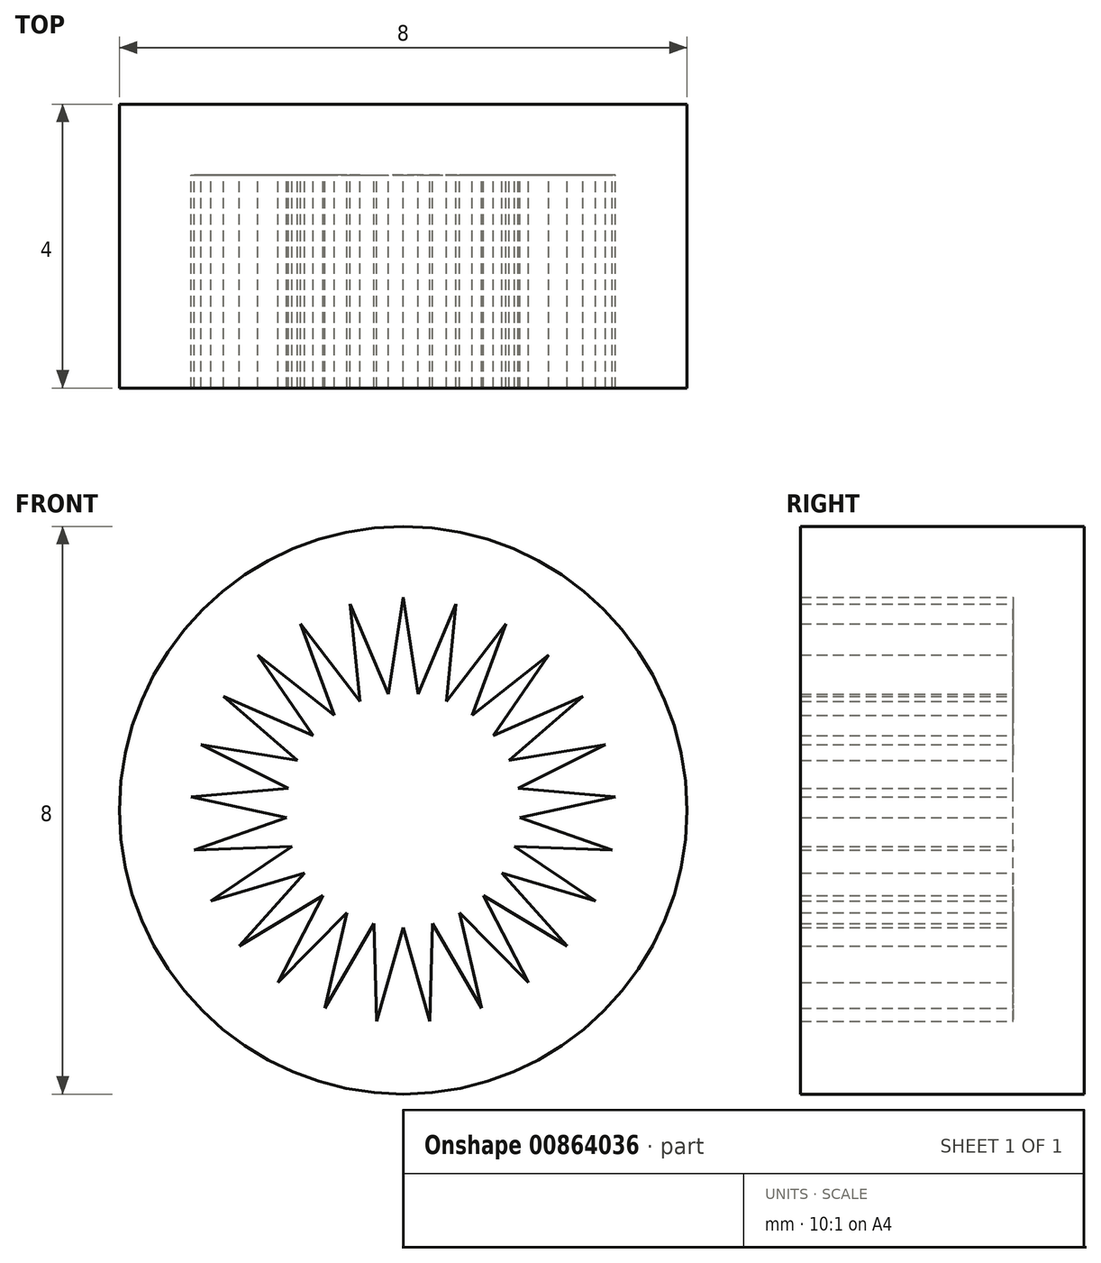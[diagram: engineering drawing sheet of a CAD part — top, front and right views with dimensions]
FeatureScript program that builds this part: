
annotation { "Feature Type Name" : "Feature", "Feature Type Description" : "" }
export const myFeature = defineFeature(function(context is Context, id is Id, definition is map)
    precondition{}
    {
        {
            var Q0;
            Q0=qCreatedBy(makeId("Front.planeOp"),FACE);
            var sketch = newSketch(context, id + "F0", { "sketchPlane" : qUnion([Q0])});
            skCircle(sketch, "E0", {"center": v(0, 0) * mm, "radius": 3 * mm});
            skCircle(sketch, "E1", {"center": v(0, 0) * mm, "radius": 4 * mm});
            skCircle(sketch, "E2", {"center": v(0, 0) * mm, "radius": 1.65 * mm});
            skCircle(sketch, "E3.cCircle", {"center": v(0, 0) * mm, "radius": 3 * mm, "construction": true});
            skCircle(sketch, "E4.cCircle", {"center": v(0, 0) * mm, "radius": 1.65 * mm, "construction": true});
            skLineSegment(sketch, "E4.0", {"start": v(0, -1.65) * mm, "end": v(-0.41, -1.6) * mm});
            skLineSegment(sketch, "E4.1", {"start": v(-0.41, -1.6) * mm, "end": v(-0.8, -1.45) * mm});
            skLineSegment(sketch, "E4.2", {"start": v(-0.8, -1.45) * mm, "end": v(-1.13, -1.2) * mm});
            skLineSegment(sketch, "E4.3", {"start": v(-1.13, -1.2) * mm, "end": v(-1.4, -0.88) * mm});
            skLineSegment(sketch, "E4.4", {"start": v(-1.4, -0.88) * mm, "end": v(-1.57, -0.5) * mm});
            skLineSegment(sketch, "E4.5", {"start": v(-1.57, -0.5) * mm, "end": v(-1.65, -0.1) * mm});
            skLineSegment(sketch, "E4.6", {"start": v(-1.65, -0.1) * mm, "end": v(-1.62, 0.3) * mm});
            skLineSegment(sketch, "E4.7", {"start": v(-1.62, 0.3) * mm, "end": v(-1.5, 0.7) * mm});
            skLineSegment(sketch, "E4.8", {"start": v(-1.5, 0.7) * mm, "end": v(-1.27, 1.05) * mm});
            skLineSegment(sketch, "E4.9", {"start": v(-1.27, 1.05) * mm, "end": v(-0.97, 1.33) * mm});
            skLineSegment(sketch, "E4.10", {"start": v(-0.97, 1.33) * mm, "end": v(-0.6, 1.53) * mm});
            skLineSegment(sketch, "E4.11", {"start": v(-0.6, 1.53) * mm, "end": v(-0.2, 1.64) * mm});
            skLineSegment(sketch, "E4.12", {"start": v(-0.2, 1.64) * mm, "end": v(0.2, 1.64) * mm});
            skLineSegment(sketch, "E4.13", {"start": v(0.2, 1.64) * mm, "end": v(0.6, 1.53) * mm});
            skLineSegment(sketch, "E4.14", {"start": v(0.6, 1.53) * mm, "end": v(0.97, 1.33) * mm});
            skLineSegment(sketch, "E4.15", {"start": v(0.97, 1.33) * mm, "end": v(1.27, 1.05) * mm});
            skLineSegment(sketch, "E4.16", {"start": v(1.27, 1.05) * mm, "end": v(1.5, 0.7) * mm});
            skLineSegment(sketch, "E4.17", {"start": v(1.5, 0.7) * mm, "end": v(1.62, 0.3) * mm});
            skLineSegment(sketch, "E4.18", {"start": v(1.62, 0.3) * mm, "end": v(1.65, -0.1) * mm});
            skLineSegment(sketch, "E4.19", {"start": v(1.65, -0.1) * mm, "end": v(1.57, -0.5) * mm});
            skLineSegment(sketch, "E4.20", {"start": v(1.57, -0.5) * mm, "end": v(1.4, -0.88) * mm});
            skLineSegment(sketch, "E4.21", {"start": v(1.4, -0.88) * mm, "end": v(1.13, -1.2) * mm});
            skLineSegment(sketch, "E4.22", {"start": v(1.13, -1.2) * mm, "end": v(0.8, -1.45) * mm});
            skLineSegment(sketch, "E4.23", {"start": v(0.8, -1.45) * mm, "end": v(0.41, -1.6) * mm});
            skLineSegment(sketch, "E4.24", {"start": v(0.41, -1.6) * mm, "end": v(0, -1.65) * mm});
            skLineSegment(sketch, "E5", {"start": v(0, 3) * mm, "end": v(-0.2, 1.64) * mm});
            skLineSegment(sketch, "E6", {"start": v(-0.75, 2.9) * mm, "end": v(-0.2, 1.64) * mm});
            skLineSegment(sketch, "E7", {"start": v(-0.75, 2.9) * mm, "end": v(-0.6, 1.53) * mm});
            skLineSegment(sketch, "E8", {"start": v(-0.6, 1.53) * mm, "end": v(-1.45, 2.63) * mm});
            skLineSegment(sketch, "E9", {"start": v(-1.45, 2.63) * mm, "end": v(-0.97, 1.33) * mm});
            skLineSegment(sketch, "E10", {"start": v(-0.97, 1.33) * mm, "end": v(-2.05, 2.19) * mm});
            skLineSegment(sketch, "E11", {"start": v(-2.05, 2.19) * mm, "end": v(-1.27, 1.05) * mm});
            skLineSegment(sketch, "E12", {"start": v(-1.27, 1.05) * mm, "end": v(-2.53, 1.6) * mm});
            skLineSegment(sketch, "E13", {"start": v(-2.53, 1.6) * mm, "end": v(-1.5, 0.7) * mm});
            skLineSegment(sketch, "E14", {"start": v(-1.5, 0.7) * mm, "end": v(-2.85, 0.93) * mm});
            skLineSegment(sketch, "E15", {"start": v(-2.85, 0.93) * mm, "end": v(-1.62, 0.3) * mm});
            skLineSegment(sketch, "E16", {"start": v(-1.62, 0.3) * mm, "end": v(-3, 0.19) * mm});
            skLineSegment(sketch, "E17", {"start": v(-3, 0.19) * mm, "end": v(-1.65, -0.1) * mm});
            skLineSegment(sketch, "E18", {"start": v(-1.65, -0.1) * mm, "end": v(-2.95, -0.56) * mm});
            skLineSegment(sketch, "E19", {"start": v(-2.95, -0.56) * mm, "end": v(-1.57, -0.5) * mm});
            skLineSegment(sketch, "E20", {"start": v(-1.57, -0.5) * mm, "end": v(-2.71, -1.28) * mm});
            skLineSegment(sketch, "E21", {"start": v(-2.71, -1.28) * mm, "end": v(-1.4, -0.88) * mm});
            skLineSegment(sketch, "E22", {"start": v(-1.4, -0.88) * mm, "end": v(-2.31, -1.91) * mm});
            skLineSegment(sketch, "E23", {"start": v(-2.31, -1.91) * mm, "end": v(-1.13, -1.2) * mm});
            skLineSegment(sketch, "E24", {"start": v(-1.13, -1.2) * mm, "end": v(-1.76, -2.43) * mm});
            skLineSegment(sketch, "E25", {"start": v(-1.76, -2.43) * mm, "end": v(-0.8, -1.45) * mm});
            skLineSegment(sketch, "E26", {"start": v(-0.8, -1.45) * mm, "end": v(-1.1, -2.79) * mm});
            skLineSegment(sketch, "E27", {"start": v(-1.1, -2.79) * mm, "end": v(-0.41, -1.6) * mm});
            skLineSegment(sketch, "E28", {"start": v(-0.41, -1.6) * mm, "end": v(-0.38, -2.98) * mm});
            skLineSegment(sketch, "E29", {"start": v(-0.38, -2.98) * mm, "end": v(0, -1.65) * mm});
            skLineSegment(sketch, "E30", {"start": v(0, -1.65) * mm, "end": v(0.38, -2.98) * mm});
            skLineSegment(sketch, "E31", {"start": v(0.38, -2.98) * mm, "end": v(0.41, -1.6) * mm});
            skLineSegment(sketch, "E32", {"start": v(0.41, -1.6) * mm, "end": v(1.1, -2.79) * mm});
            skLineSegment(sketch, "E33", {"start": v(1.1, -2.79) * mm, "end": v(0.8, -1.45) * mm});
            skLineSegment(sketch, "E34", {"start": v(0.8, -1.45) * mm, "end": v(1.76, -2.43) * mm});
            skLineSegment(sketch, "E35", {"start": v(1.76, -2.43) * mm, "end": v(1.13, -1.2) * mm});
            skLineSegment(sketch, "E36", {"start": v(1.13, -1.2) * mm, "end": v(2.31, -1.91) * mm});
            skLineSegment(sketch, "E37", {"start": v(2.31, -1.91) * mm, "end": v(1.4, -0.88) * mm});
            skLineSegment(sketch, "E38", {"start": v(1.4, -0.88) * mm, "end": v(2.71, -1.28) * mm});
            skLineSegment(sketch, "E39", {"start": v(2.71, -1.28) * mm, "end": v(1.57, -0.5) * mm});
            skLineSegment(sketch, "E40", {"start": v(1.57, -0.5) * mm, "end": v(2.95, -0.56) * mm});
            skLineSegment(sketch, "E41", {"start": v(2.95, -0.56) * mm, "end": v(1.65, -0.1) * mm});
            skLineSegment(sketch, "E42", {"start": v(1.65, -0.1) * mm, "end": v(3, 0.19) * mm});
            skLineSegment(sketch, "E43", {"start": v(3, 0.19) * mm, "end": v(1.62, 0.3) * mm});
            skLineSegment(sketch, "E44", {"start": v(1.62, 0.3) * mm, "end": v(2.85, 0.93) * mm});
            skLineSegment(sketch, "E45", {"start": v(2.85, 0.93) * mm, "end": v(1.5, 0.7) * mm});
            skLineSegment(sketch, "E46", {"start": v(1.5, 0.7) * mm, "end": v(2.53, 1.6) * mm});
            skLineSegment(sketch, "E47", {"start": v(2.53, 1.6) * mm, "end": v(1.27, 1.05) * mm});
            skLineSegment(sketch, "E48", {"start": v(1.27, 1.05) * mm, "end": v(2.05, 2.19) * mm});
            skLineSegment(sketch, "E49", {"start": v(2.05, 2.19) * mm, "end": v(0.97, 1.33) * mm});
            skLineSegment(sketch, "E50", {"start": v(0.97, 1.33) * mm, "end": v(1.45, 2.63) * mm});
            skLineSegment(sketch, "E51", {"start": v(1.45, 2.63) * mm, "end": v(0.6, 1.53) * mm});
            skLineSegment(sketch, "E52", {"start": v(0.6, 1.53) * mm, "end": v(0.75, 2.9) * mm});
            skLineSegment(sketch, "E53", {"start": v(0.75, 2.9) * mm, "end": v(0.2, 1.64) * mm});
            skLineSegment(sketch, "E54", {"start": v(0.2, 1.64) * mm, "end": v(0, 3) * mm});
            skSolve(sketch);
        }
        {
            var Q0;
            Q0=makeQuery(id+"F0.imprint","IMPRINT",FACE,{"disambiguationData":[TD([[makeQuery(id+"F0.imprint","IMPRINT",EDGE,{"derivedFrom":sQuery(id+"F0.wireOp",EDGE,"E1")}),1.0]])]});
            var Q1;
            {var subQ0=sQuery(id+"F0.wireOp",EDGE,"191f228b-e5a5-47d5-a300-bf6d3b310172");Q1=makeQuery(id+"F0.imprint","IMPRINT",FACE,{"disambiguationData":[TD([[makeQuery(id+"F0.imprint","IMPRINT",EDGE,{"derivedFrom":subQ0}),-1.0]])]});}
            var Q2;
            {var subQ0=sQuery(id+"F0.wireOp",EDGE,"1723c25a-e232-420a-af23-11f6e1e45479");Q2=makeQuery(id+"F0.imprint","IMPRINT",FACE,{"disambiguationData":[TD([[makeQuery(id+"F0.imprint","IMPRINT",EDGE,{"derivedFrom":subQ0}),-1.0]])]});}
            var Q3;
            {var subQ0=sQuery(id+"F0.wireOp",EDGE,"362b071b-b4e2-4c32-97d3-f70041ff60b6");Q3=makeQuery(id+"F0.imprint","IMPRINT",FACE,{"disambiguationData":[TD([[makeQuery(id+"F0.imprint","IMPRINT",EDGE,{"derivedFrom":subQ0}),1.0]])]});}
            var Q4;
            {var subQ0=sQuery(id+"F0.wireOp",EDGE,"7a3e42e3-73c9-4e71-a878-db48f86a027f");Q4=makeQuery(id+"F0.imprint","IMPRINT",FACE,{"disambiguationData":[TD([[makeQuery(id+"F0.imprint","IMPRINT",EDGE,{"derivedFrom":subQ0}),1.0]])]});}
            var Q5;
            {var subQ0=sQuery(id+"F0.wireOp",EDGE,"a710b964-fec3-4947-b213-2410728157db");Q5=makeQuery(id+"F0.imprint","IMPRINT",FACE,{"disambiguationData":[TD([[makeQuery(id+"F0.imprint","IMPRINT",EDGE,{"derivedFrom":subQ0}),1.0]])]});}
            var Q6;
            {var subQ0=sQuery(id+"F0.wireOp",EDGE,"60680273-4920-44da-8bc3-3f6f87752808");Q6=makeQuery(id+"F0.imprint","IMPRINT",FACE,{"disambiguationData":[TD([[makeQuery(id+"F0.imprint","IMPRINT",EDGE,{"derivedFrom":subQ0}),1.0]])]});}
            var Q7;
            {var subQ0=sQuery(id+"F0.wireOp",EDGE,"2f8d73f0-317a-4c88-aaee-1b2851b7c96e");Q7=makeQuery(id+"F0.imprint","IMPRINT",FACE,{"disambiguationData":[TD([[makeQuery(id+"F0.imprint","IMPRINT",EDGE,{"derivedFrom":subQ0}),1.0]])]});}
            var Q8;
            {var subQ0=sQuery(id+"F0.wireOp",EDGE,"349960dc-c3b8-4aa2-95a6-2044da98fb72");Q8=makeQuery(id+"F0.imprint","IMPRINT",FACE,{"disambiguationData":[TD([[makeQuery(id+"F0.imprint","IMPRINT",EDGE,{"derivedFrom":subQ0}),1.0]])]});}
            var Q9;
            {var subQ0=sQuery(id+"F0.wireOp",EDGE,"c7be37dc-6ee6-451d-a77f-0cf4add8b74c");Q9=makeQuery(id+"F0.imprint","IMPRINT",FACE,{"disambiguationData":[TD([[makeQuery(id+"F0.imprint","IMPRINT",EDGE,{"derivedFrom":subQ0}),1.0]])]});}
            var Q10;
            {var subQ0=sQuery(id+"F0.wireOp",EDGE,"4aff2ad2-ea2a-4098-8c14-60c1d9ab17a0");Q10=makeQuery(id+"F0.imprint","IMPRINT",FACE,{"disambiguationData":[TD([[makeQuery(id+"F0.imprint","IMPRINT",EDGE,{"derivedFrom":subQ0}),-1.0]])]});}
            var Q11;
            {var subQ0=sQuery(id+"F0.wireOp",EDGE,"2e92db5d-52d9-4a2f-acd0-dec73ec550c8");Q11=makeQuery(id+"F0.imprint","IMPRINT",FACE,{"disambiguationData":[TD([[makeQuery(id+"F0.imprint","IMPRINT",EDGE,{"derivedFrom":subQ0}),-1.0]])]});}
            var Q12;
            {var subQ0=sQuery(id+"F0.wireOp",EDGE,"9941dce6-5cf8-40e4-90cd-53aa257fbfa3");Q12=makeQuery(id+"F0.imprint","IMPRINT",FACE,{"disambiguationData":[TD([[makeQuery(id+"F0.imprint","IMPRINT",EDGE,{"derivedFrom":subQ0}),-1.0]])]});}
            var Q13;
            {var subQ2=sQuery(id+"F0.wireOp",EDGE,"aa89b7cd-d551-4e84-b0b1-1e06fde4f388");Q13=makeQuery(id+"F0.imprint","IMPRINT",FACE,{"disambiguationData":[TD([[makeQuery(id+"F0.imprint","IMPRINT",EDGE,{"derivedFrom":subQ2}),1.0]])]});}
            var Q14;
            {var subQ0=sQuery(id+"F0.wireOp",EDGE,"cc53d425-3ef8-4edf-87f2-34f36bc6dec7");Q14=makeQuery(id+"F0.imprint","IMPRINT",FACE,{"disambiguationData":[TD([[makeQuery(id+"F0.imprint","IMPRINT",EDGE,{"derivedFrom":subQ0}),1.0]])]});}
            var Q15;
            {var subQ0=sQuery(id+"F0.wireOp",EDGE,"99681175-5654-4388-8651-d3d52a13e443");Q15=makeQuery(id+"F0.imprint","IMPRINT",FACE,{"disambiguationData":[TD([[makeQuery(id+"F0.imprint","IMPRINT",EDGE,{"derivedFrom":subQ0}),1.0]])]});}
            var Q16;
            {var subQ0=sQuery(id+"F0.wireOp",EDGE,"2ca4b1c5-08c9-43bc-8a30-41003a56ef57");Q16=makeQuery(id+"F0.imprint","IMPRINT",FACE,{"disambiguationData":[TD([[makeQuery(id+"F0.imprint","IMPRINT",EDGE,{"derivedFrom":subQ0}),1.0]])]});}
            var Q17;
            {var subQ0=sQuery(id+"F0.wireOp",EDGE,"d3c2645e-955d-4a5b-9ae6-9eed4a245719");Q17=makeQuery(id+"F0.imprint","IMPRINT",FACE,{"disambiguationData":[TD([[makeQuery(id+"F0.imprint","IMPRINT",EDGE,{"derivedFrom":subQ0}),1.0]])]});}
            var Q18;
            {var subQ0=sQuery(id+"F0.wireOp",EDGE,"d3f6a87d-8e7b-4a19-8049-f323434571ec");Q18=makeQuery(id+"F0.imprint","IMPRINT",FACE,{"disambiguationData":[TD([[makeQuery(id+"F0.imprint","IMPRINT",EDGE,{"derivedFrom":subQ0}),1.0]])]});}
            var Q19;
            {var subQ0=sQuery(id+"F0.wireOp",EDGE,"589032c6-bdc8-48a5-8756-f54bf3a24945");Q19=makeQuery(id+"F0.imprint","IMPRINT",FACE,{"disambiguationData":[TD([[makeQuery(id+"F0.imprint","IMPRINT",EDGE,{"derivedFrom":subQ0}),1.0]])]});}
            var Q20;
            {var subQ0=sQuery(id+"F0.wireOp",EDGE,"12f93d1c-aee5-4c1c-92fe-329b828fc1ab");Q20=makeQuery(id+"F0.imprint","IMPRINT",FACE,{"disambiguationData":[TD([[makeQuery(id+"F0.imprint","IMPRINT",EDGE,{"derivedFrom":subQ0}),1.0]])]});}
            var Q21;
            {var subQ0=sQuery(id+"F0.wireOp",EDGE,"b9c6a9d8-4597-4bf0-9964-2ef2b3ef8dc4");Q21=makeQuery(id+"F0.imprint","IMPRINT",FACE,{"disambiguationData":[TD([[makeQuery(id+"F0.imprint","IMPRINT",EDGE,{"derivedFrom":subQ0}),1.0]])]});}
            var Q22;
            {var subQ0=sQuery(id+"F0.wireOp",EDGE,"6288aacb-8e0d-4685-9329-790f9a596c2f");Q22=makeQuery(id+"F0.imprint","IMPRINT",FACE,{"disambiguationData":[TD([[makeQuery(id+"F0.imprint","IMPRINT",EDGE,{"derivedFrom":subQ0}),1.0]])]});}
            var Q23;
            {var subQ0=sQuery(id+"F0.wireOp",EDGE,"50311a24-d9df-4292-b5ea-d22f6d0c8ad2");Q23=makeQuery(id+"F0.imprint","IMPRINT",FACE,{"disambiguationData":[TD([[makeQuery(id+"F0.imprint","IMPRINT",EDGE,{"derivedFrom":subQ0}),1.0]])]});}
            var Q24;
            {var subQ0=sQuery(id+"F0.wireOp",EDGE,"c8f29483-0d33-4b23-b36e-bf183a1a309b");Q24=makeQuery(id+"F0.imprint","IMPRINT",FACE,{"disambiguationData":[TD([[makeQuery(id+"F0.imprint","IMPRINT",EDGE,{"derivedFrom":subQ0}),1.0]])]});}
            var Q25;
            {var subQ0=sQuery(id+"F0.wireOp",EDGE,"e2a48b54-4f9e-43bf-ae69-ea60452bf6d6");Q25=makeQuery(id+"F0.imprint","IMPRINT",FACE,{"disambiguationData":[TD([[makeQuery(id+"F0.imprint","IMPRINT",EDGE,{"derivedFrom":subQ0}),1.0]])]});}
            var Q26;
            Q26=makeQuery(id+"F0.imprint","IMPRINT",FACE,{"disambiguationData":[TD([[makeQuery(id+"F0.imprint","IMPRINT",EDGE,{"derivedFrom":sQuery(id+"F0.wireOp",EDGE,"E3.19")}),-1.0]])]});
            var Q27;
            Q27=makeQuery(id+"F0.imprint","IMPRINT",FACE,{"disambiguationData":[TD([[makeQuery(id+"F0.imprint","IMPRINT",EDGE,{"derivedFrom":sQuery(id+"F0.wireOp",EDGE,"E3.18")}),-1.0]])]});
            var Q28;
            Q28=makeQuery(id+"F0.imprint","IMPRINT",FACE,{"disambiguationData":[TD([[makeQuery(id+"F0.imprint","IMPRINT",EDGE,{"derivedFrom":sQuery(id+"F0.wireOp",EDGE,"E3.21")}),-1.0]])]});
            var Q29;
            Q29=makeQuery(id+"F0.imprint","IMPRINT",FACE,{"disambiguationData":[TD([[makeQuery(id+"F0.imprint","IMPRINT",EDGE,{"derivedFrom":sQuery(id+"F0.wireOp",EDGE,"E3.22")}),-1.0]])]});
            var Q30;
            Q30=makeQuery(id+"F0.imprint","IMPRINT",FACE,{"disambiguationData":[TD([[makeQuery(id+"F0.imprint","IMPRINT",EDGE,{"derivedFrom":sQuery(id+"F0.wireOp",EDGE,"E3.23")}),-1.0]])]});
            var Q31;
            Q31=makeQuery(id+"F0.imprint","IMPRINT",FACE,{"disambiguationData":[TD([[makeQuery(id+"F0.imprint","IMPRINT",EDGE,{"derivedFrom":sQuery(id+"F0.wireOp",EDGE,"E3.20")}),-1.0]])]});
            var Q32;
            Q32=makeQuery(id+"F0.imprint","IMPRINT",FACE,{"disambiguationData":[TD([[makeQuery(id+"F0.imprint","IMPRINT",EDGE,{"derivedFrom":sQuery(id+"F0.wireOp",EDGE,"E3.17")}),-1.0]])]});
            var Q33;
            Q33=makeQuery(id+"F0.imprint","IMPRINT",FACE,{"disambiguationData":[TD([[makeQuery(id+"F0.imprint","IMPRINT",EDGE,{"derivedFrom":sQuery(id+"F0.wireOp",EDGE,"E3.15")}),-1.0]])]});
            var Q34;
            Q34=makeQuery(id+"F0.imprint","IMPRINT",FACE,{"disambiguationData":[TD([[makeQuery(id+"F0.imprint","IMPRINT",EDGE,{"derivedFrom":sQuery(id+"F0.wireOp",EDGE,"E3.16")}),-1.0]])]});
            var Q35;
            Q35=makeQuery(id+"F0.imprint","IMPRINT",FACE,{"disambiguationData":[TD([[makeQuery(id+"F0.imprint","IMPRINT",EDGE,{"derivedFrom":sQuery(id+"F0.wireOp",EDGE,"E3.14")}),-1.0]])]});
            var Q36;
            Q36=makeQuery(id+"F0.imprint","IMPRINT",FACE,{"disambiguationData":[TD([[makeQuery(id+"F0.imprint","IMPRINT",EDGE,{"derivedFrom":sQuery(id+"F0.wireOp",EDGE,"E3.13")}),-1.0]])]});
            var Q37;
            Q37=makeQuery(id+"F0.imprint","IMPRINT",FACE,{"disambiguationData":[TD([[makeQuery(id+"F0.imprint","IMPRINT",EDGE,{"derivedFrom":sQuery(id+"F0.wireOp",EDGE,"E3.12")}),-1.0]])]});
            var Q38;
            Q38=makeQuery(id+"F0.imprint","IMPRINT",FACE,{"disambiguationData":[TD([[makeQuery(id+"F0.imprint","IMPRINT",EDGE,{"derivedFrom":sQuery(id+"F0.wireOp",EDGE,"E3.11")}),-1.0]])]});
            var Q39;
            Q39=makeQuery(id+"F0.imprint","IMPRINT",FACE,{"disambiguationData":[TD([[makeQuery(id+"F0.imprint","IMPRINT",EDGE,{"derivedFrom":sQuery(id+"F0.wireOp",EDGE,"E3.10")}),-1.0]])]});
            var Q40;
            Q40=makeQuery(id+"F0.imprint","IMPRINT",FACE,{"disambiguationData":[TD([[makeQuery(id+"F0.imprint","IMPRINT",EDGE,{"derivedFrom":sQuery(id+"F0.wireOp",EDGE,"E3.9")}),-1.0]])]});
            var Q41;
            Q41=makeQuery(id+"F0.imprint","IMPRINT",FACE,{"disambiguationData":[TD([[makeQuery(id+"F0.imprint","IMPRINT",EDGE,{"derivedFrom":sQuery(id+"F0.wireOp",EDGE,"E3.8")}),-1.0]])]});
            var Q42;
            Q42=makeQuery(id+"F0.imprint","IMPRINT",FACE,{"disambiguationData":[TD([[makeQuery(id+"F0.imprint","IMPRINT",EDGE,{"derivedFrom":sQuery(id+"F0.wireOp",EDGE,"E3.7")}),-1.0]])]});
            var Q43;
            Q43=makeQuery(id+"F0.imprint","IMPRINT",FACE,{"disambiguationData":[TD([[makeQuery(id+"F0.imprint","IMPRINT",EDGE,{"derivedFrom":sQuery(id+"F0.wireOp",EDGE,"E3.6")}),-1.0]])]});
            var Q44;
            Q44=makeQuery(id+"F0.imprint","IMPRINT",FACE,{"disambiguationData":[TD([[makeQuery(id+"F0.imprint","IMPRINT",EDGE,{"derivedFrom":sQuery(id+"F0.wireOp",EDGE,"E3.5")}),-1.0]])]});
            var Q45;
            Q45=makeQuery(id+"F0.imprint","IMPRINT",FACE,{"disambiguationData":[TD([[makeQuery(id+"F0.imprint","IMPRINT",EDGE,{"derivedFrom":sQuery(id+"F0.wireOp",EDGE,"E3.4")}),-1.0]])]});
            var Q46;
            Q46=makeQuery(id+"F0.imprint","IMPRINT",FACE,{"disambiguationData":[TD([[makeQuery(id+"F0.imprint","IMPRINT",EDGE,{"derivedFrom":sQuery(id+"F0.wireOp",EDGE,"E3.3")}),-1.0]])]});
            var Q47;
            Q47=makeQuery(id+"F0.imprint","IMPRINT",FACE,{"disambiguationData":[TD([[makeQuery(id+"F0.imprint","IMPRINT",EDGE,{"derivedFrom":sQuery(id+"F0.wireOp",EDGE,"E3.2")}),-1.0]])]});
            var Q48;
            Q48=makeQuery(id+"F0.imprint","IMPRINT",FACE,{"disambiguationData":[TD([[makeQuery(id+"F0.imprint","IMPRINT",EDGE,{"derivedFrom":sQuery(id+"F0.wireOp",EDGE,"E3.0")}),-1.0]])]});
            var Q49;
            Q49=makeQuery(id+"F0.imprint","IMPRINT",FACE,{"disambiguationData":[TD([[makeQuery(id+"F0.imprint","IMPRINT",EDGE,{"derivedFrom":sQuery(id+"F0.wireOp",EDGE,"E3.24")}),-1.0]])]});
            var Q50;
            Q50=makeQuery(id+"F0.imprint","IMPRINT",FACE,{"disambiguationData":[TD([[makeQuery(id+"F0.imprint","IMPRINT",EDGE,{"derivedFrom":sQuery(id+"F0.wireOp",EDGE,"E3.1")}),-1.0]])]});
            var Q51;
            {var subQ0=sQuery(id+"F0.wireOp",EDGE,"E7");Q51=makeQuery(id+"F0.imprint","IMPRINT",FACE,{"disambiguationData":[TD([[makeQuery(id+"F0.imprint","IMPRINT",EDGE,{"derivedFrom":subQ0}),-1.0]])]});}
            var Q52;
            {var subQ0=sQuery(id+"F0.wireOp",EDGE,"E9");Q52=makeQuery(id+"F0.imprint","IMPRINT",FACE,{"disambiguationData":[TD([[makeQuery(id+"F0.imprint","IMPRINT",EDGE,{"derivedFrom":subQ0}),-1.0]])]});}
            var Q53;
            {var subQ0=sQuery(id+"F0.wireOp",EDGE,"E11");Q53=makeQuery(id+"F0.imprint","IMPRINT",FACE,{"disambiguationData":[TD([[makeQuery(id+"F0.imprint","IMPRINT",EDGE,{"derivedFrom":subQ0}),-1.0]])]});}
            var Q54;
            {var subQ0=sQuery(id+"F0.wireOp",EDGE,"E5");Q54=makeQuery(id+"F0.imprint","IMPRINT",FACE,{"disambiguationData":[TD([[makeQuery(id+"F0.imprint","IMPRINT",EDGE,{"derivedFrom":subQ0}),-1.0]])]});}
            var Q55;
            {var subQ2=sQuery(id+"F0.wireOp",EDGE,"E53");Q55=makeQuery(id+"F0.imprint","IMPRINT",FACE,{"disambiguationData":[TD([[makeQuery(id+"F0.imprint","IMPRINT",EDGE,{"derivedFrom":subQ2}),-1.0]])]});}
            var Q56;
            {var subQ0=sQuery(id+"F0.wireOp",EDGE,"E51");Q56=makeQuery(id+"F0.imprint","IMPRINT",FACE,{"disambiguationData":[TD([[makeQuery(id+"F0.imprint","IMPRINT",EDGE,{"derivedFrom":subQ0}),-1.0]])]});}
            var Q57;
            {var subQ0=sQuery(id+"F0.wireOp",EDGE,"E49");Q57=makeQuery(id+"F0.imprint","IMPRINT",FACE,{"disambiguationData":[TD([[makeQuery(id+"F0.imprint","IMPRINT",EDGE,{"derivedFrom":subQ0}),-1.0]])]});}
            extrude(context, id + "F1", {"entities" : qUnion([Q0, Q1, Q2, Q3, Q4, Q5, Q6, Q7, Q8, Q9, Q10, Q11, Q12, Q13, Q14, Q15, Q16, Q17, Q18, Q19, Q20, Q21, Q22, Q23, Q24, Q25, Q26, Q27, Q28, Q29, Q30, Q31, Q32, Q33, Q34, Q35, Q36, Q37, Q38, Q39, Q40, Q41, Q42, Q43, Q44, Q45, Q46, Q47, Q48, Q49, Q50, Q51, Q52, Q53, Q54, Q55, Q56, Q57]), "depth" : 3 * mm, "offsetDistance" : 25 * mm});
        }
        {
            var Q0;
            Q0=makeQuery(id+"F1.opExtrude","SWEPT_BODY",BODY,{"disambiguationData":[OSD([sQuery(id+"F0.wireOp",EDGE,"1723c25a-e232-420a-af23-11f6e1e45479"),sQuery(id+"F0.wireOp",EDGE,"5295c6c6-52b0-4e9a-9c64-aa566c587db1"),sQuery(id+"F0.wireOp",EDGE,"191f228b-e5a5-47d5-a300-bf6d3b310172"),sQuery(id+"F0.wireOp",EDGE,"cf70ef10-be83-42a8-b998-76c03f429467"),sQuery(id+"F0.wireOp",EDGE,"2e92db5d-52d9-4a2f-acd0-dec73ec550c8"),sQuery(id+"F0.wireOp",EDGE,"8a1419a8-a6e0-4fe3-8ad0-2659a204953f"),sQuery(id+"F0.wireOp",EDGE,"9941dce6-5cf8-40e4-90cd-53aa257fbfa3"),sQuery(id+"F0.wireOp",EDGE,"38f36d66-5889-4d61-b17e-66de369334f1"),sQuery(id+"F0.wireOp",EDGE,"362b071b-b4e2-4c32-97d3-f70041ff60b6"),sQuery(id+"F0.wireOp",EDGE,"a209e0ad-c9d0-4362-9147-c419651424fc"),sQuery(id+"F0.wireOp",EDGE,"7a3e42e3-73c9-4e71-a878-db48f86a027f"),sQuery(id+"F0.wireOp",EDGE,"a177d376-87b9-463b-93ab-41dd6348bae0"),sQuery(id+"F0.wireOp",EDGE,"a710b964-fec3-4947-b213-2410728157db"),sQuery(id+"F0.wireOp",EDGE,"1ebe16a6-329b-423c-8d02-a690ea02e21a"),sQuery(id+"F0.wireOp",EDGE,"60680273-4920-44da-8bc3-3f6f87752808"),sQuery(id+"F0.wireOp",EDGE,"07a1d955-efb7-4b04-82f9-21b5b055ff9c"),sQuery(id+"F0.wireOp",EDGE,"2f8d73f0-317a-4c88-aaee-1b2851b7c96e"),sQuery(id+"F0.wireOp",EDGE,"177c940f-3e80-47e4-9597-e37eb8e28c60"),sQuery(id+"F0.wireOp",EDGE,"349960dc-c3b8-4aa2-95a6-2044da98fb72"),sQuery(id+"F0.wireOp",EDGE,"f5aa7e73-0121-4040-9320-5db813b2d3bf"),sQuery(id+"F0.wireOp",EDGE,"c7be37dc-6ee6-451d-a77f-0cf4add8b74c"),sQuery(id+"F0.wireOp",EDGE,"97bad7f0-ba5f-4ffa-8f54-a637fe049995"),sQuery(id+"F0.wireOp",EDGE,"4aff2ad2-ea2a-4098-8c14-60c1d9ab17a0"),sQuery(id+"F0.wireOp",EDGE,"d753e143-b6aa-4dee-8de6-cae75ad036f2"),sQuery(id+"F0.wireOp",EDGE,"c8f29483-0d33-4b23-b36e-bf183a1a309b"),sQuery(id+"F0.wireOp",EDGE,"5b43d50d-1a8e-48e3-af0a-1195e99f841e"),sQuery(id+"F0.wireOp",EDGE,"e2a48b54-4f9e-43bf-ae69-ea60452bf6d6"),sQuery(id+"F0.wireOp",EDGE,"42233fef-6dd1-45c1-8fd8-0da537e6c1f3"),sQuery(id+"F0.wireOp",EDGE,"50311a24-d9df-4292-b5ea-d22f6d0c8ad2"),sQuery(id+"F0.wireOp",EDGE,"ddcee8d9-d30e-4910-9338-453dcf5c318e"),sQuery(id+"F0.wireOp",EDGE,"6288aacb-8e0d-4685-9329-790f9a596c2f"),sQuery(id+"F0.wireOp",EDGE,"b9c6a9d8-4597-4bf0-9964-2ef2b3ef8dc4"),sQuery(id+"F0.wireOp",EDGE,"9c044d92-1709-44a8-9e80-cc68e6d8e250"),sQuery(id+"F0.wireOp",EDGE,"7d94632d-f1b4-4678-813c-0d22cf0914ea"),sQuery(id+"F0.wireOp",EDGE,"12f93d1c-aee5-4c1c-92fe-329b828fc1ab"),sQuery(id+"F0.wireOp",EDGE,"b0bde724-e130-4cb4-bfe0-c640ccf8bd66"),sQuery(id+"F0.wireOp",EDGE,"589032c6-bdc8-48a5-8756-f54bf3a24945"),sQuery(id+"F0.wireOp",EDGE,"6b624495-a022-44ef-bb31-4b2f9aca960f"),sQuery(id+"F0.wireOp",EDGE,"d3f6a87d-8e7b-4a19-8049-f323434571ec"),sQuery(id+"F0.wireOp",EDGE,"bc16c7f2-d393-49ba-aa83-d674c351c39c"),sQuery(id+"F0.wireOp",EDGE,"d3c2645e-955d-4a5b-9ae6-9eed4a245719"),sQuery(id+"F0.wireOp",EDGE,"6b5cc574-cdc1-46be-bbed-f7c8129c668f"),sQuery(id+"F0.wireOp",EDGE,"2ca4b1c5-08c9-43bc-8a30-41003a56ef57"),sQuery(id+"F0.wireOp",EDGE,"21c57bb4-7a4b-46c3-846a-edf095b63d1c"),sQuery(id+"F0.wireOp",EDGE,"99681175-5654-4388-8651-d3d52a13e443"),sQuery(id+"F0.wireOp",EDGE,"40837eb8-84b9-4c3f-ab84-b3bfe63bb642"),sQuery(id+"F0.wireOp",EDGE,"cc53d425-3ef8-4edf-87f2-34f36bc6dec7"),sQuery(id+"F0.wireOp",EDGE,"33acad9c-a8be-4903-80bc-ac94ea259cea"),sQuery(id+"F0.wireOp",EDGE,"aa89b7cd-d551-4e84-b0b1-1e06fde4f388"),sQuery(id+"F0.wireOp",EDGE,"749e164d-3242-49c0-9532-238b60e44d8e"),sQuery(id+"F0.wireOp",EDGE,"E1")])]});
            var Q1;
            Q1=qCreatedBy(makeId("Origin.pointOp"),VERTEX);
            transform(context, id + "F2", {"entities" : qUnion([Q0]), "transformType" : TransformType.SCALE_UNIFORMLY, "scale" : 1, "scalePoint" : qUnion([Q1]), "makeCopy" : false});
        }
        {
            var Q0;
            Q0=makeQuery(id+"F0.imprint","IMPRINT",FACE,{"disambiguationData":[TD([[makeQuery(id+"F0.imprint","IMPRINT",EDGE,{"derivedFrom":sQuery(id+"F0.wireOp",EDGE,"E1")}),1.0]])]});
            var Q1;
            {var subQ3=sQuery(id+"F0.wireOp",EDGE,"E24");Q1=makeQuery(id+"F0.imprint","IMPRINT",FACE,{"disambiguationData":[TD([[makeQuery(id+"F0.imprint","IMPRINT",EDGE,{"derivedFrom":subQ3}),1.0]])]});}
            var Q2;
            {var subQ3=sQuery(id+"F0.wireOp",EDGE,"E36");Q2=makeQuery(id+"F0.imprint","IMPRINT",FACE,{"disambiguationData":[TD([[makeQuery(id+"F0.imprint","IMPRINT",EDGE,{"derivedFrom":subQ3}),1.0]])]});}
            var Q3;
            {var subQ3=sQuery(id+"F0.wireOp",EDGE,"E20");Q3=makeQuery(id+"F0.imprint","IMPRINT",FACE,{"disambiguationData":[TD([[makeQuery(id+"F0.imprint","IMPRINT",EDGE,{"derivedFrom":subQ3}),1.0]])]});}
            var Q4;
            {var subQ3=sQuery(id+"F0.wireOp",EDGE,"E38");Q4=makeQuery(id+"F0.imprint","IMPRINT",FACE,{"disambiguationData":[TD([[makeQuery(id+"F0.imprint","IMPRINT",EDGE,{"derivedFrom":subQ3}),1.0]])]});}
            var Q5;
            Q5=makeQuery(id+"F0.imprint","IMPRINT",FACE,{"disambiguationData":[TD([[makeQuery(id+"F0.imprint","IMPRINT",EDGE,{"derivedFrom":sQuery(id+"F0.wireOp",EDGE,"E4.0")}),-1.0]])]});
            var Q6;
            {var subQ3=sQuery(id+"F0.wireOp",EDGE,"E18");Q6=makeQuery(id+"F0.imprint","IMPRINT",FACE,{"disambiguationData":[TD([[makeQuery(id+"F0.imprint","IMPRINT",EDGE,{"derivedFrom":subQ3}),1.0]])]});}
            var Q7;
            {var subQ0=sQuery(id+"F0.wireOp",EDGE,"E30");Q7=makeQuery(id+"F0.imprint","IMPRINT",FACE,{"disambiguationData":[TD([[makeQuery(id+"F0.imprint","IMPRINT",EDGE,{"derivedFrom":subQ0}),1.0]])]});}
            var Q8;
            {var subQ3=sQuery(id+"F0.wireOp",EDGE,"E40");Q8=makeQuery(id+"F0.imprint","IMPRINT",FACE,{"disambiguationData":[TD([[makeQuery(id+"F0.imprint","IMPRINT",EDGE,{"derivedFrom":subQ3}),1.0]])]});}
            var Q9;
            {var subQ3=sQuery(id+"F0.wireOp",EDGE,"E22");Q9=makeQuery(id+"F0.imprint","IMPRINT",FACE,{"disambiguationData":[TD([[makeQuery(id+"F0.imprint","IMPRINT",EDGE,{"derivedFrom":subQ3}),1.0]])]});}
            var Q10;
            {var subQ3=sQuery(id+"F0.wireOp",EDGE,"E16");Q10=makeQuery(id+"F0.imprint","IMPRINT",FACE,{"disambiguationData":[TD([[makeQuery(id+"F0.imprint","IMPRINT",EDGE,{"derivedFrom":subQ3}),1.0]])]});}
            var Q11;
            {var subQ3=sQuery(id+"F0.wireOp",EDGE,"E34");Q11=makeQuery(id+"F0.imprint","IMPRINT",FACE,{"disambiguationData":[TD([[makeQuery(id+"F0.imprint","IMPRINT",EDGE,{"derivedFrom":subQ3}),1.0]])]});}
            var Q12;
            {var subQ3=sQuery(id+"F0.wireOp",EDGE,"E42");Q12=makeQuery(id+"F0.imprint","IMPRINT",FACE,{"disambiguationData":[TD([[makeQuery(id+"F0.imprint","IMPRINT",EDGE,{"derivedFrom":subQ3}),1.0]])]});}
            var Q13;
            {var subQ3=sQuery(id+"F0.wireOp",EDGE,"E32");Q13=makeQuery(id+"F0.imprint","IMPRINT",FACE,{"disambiguationData":[TD([[makeQuery(id+"F0.imprint","IMPRINT",EDGE,{"derivedFrom":subQ3}),1.0]])]});}
            var Q14;
            Q14=makeQuery(id+"F1.opExtrude","CAP_FACE",FACE,{"disambiguationData":[OSD([sQuery(id+"F0.wireOp",EDGE,"E0"),sQuery(id+"F0.wireOp",EDGE,"E1")])],"isStart":true});
            var Q15;
            {var subQ0=sQuery(id+"F0.wireOp",EDGE,"E4.23");Q15=makeQuery(id+"F0.imprint","IMPRINT",FACE,{"disambiguationData":[TD([[makeQuery(id+"F0.imprint","IMPRINT",EDGE,{"derivedFrom":subQ0}),1.0]])]});}
            var Q16;
            {var subQ0=sQuery(id+"F0.wireOp",EDGE,"E4.1");Q16=makeQuery(id+"F0.imprint","IMPRINT",FACE,{"disambiguationData":[TD([[makeQuery(id+"F0.imprint","IMPRINT",EDGE,{"derivedFrom":subQ0}),1.0]])]});}
            var Q17;
            {var subQ3=sQuery(id+"F0.wireOp",EDGE,"E48");Q17=makeQuery(id+"F0.imprint","IMPRINT",FACE,{"disambiguationData":[TD([[makeQuery(id+"F0.imprint","IMPRINT",EDGE,{"derivedFrom":subQ3}),1.0]])]});}
            var Q18;
            {var subQ0=sQuery(id+"F0.wireOp",EDGE,"E4.0");Q18=makeQuery(id+"F0.imprint","IMPRINT",FACE,{"disambiguationData":[TD([[makeQuery(id+"F0.imprint","IMPRINT",EDGE,{"derivedFrom":subQ0}),1.0]])]});}
            var Q19;
            {var subQ3=sQuery(id+"F0.wireOp",EDGE,"E50");Q19=makeQuery(id+"F0.imprint","IMPRINT",FACE,{"disambiguationData":[TD([[makeQuery(id+"F0.imprint","IMPRINT",EDGE,{"derivedFrom":subQ3}),1.0]])]});}
            var Q20;
            {var subQ0=sQuery(id+"F0.wireOp",EDGE,"E4.3");Q20=makeQuery(id+"F0.imprint","IMPRINT",FACE,{"disambiguationData":[TD([[makeQuery(id+"F0.imprint","IMPRINT",EDGE,{"derivedFrom":subQ0}),1.0]])]});}
            var Q21;
            {var subQ0=sQuery(id+"F0.wireOp",EDGE,"E5");Q21=makeQuery(id+"F0.imprint","IMPRINT",FACE,{"disambiguationData":[TD([[makeQuery(id+"F0.imprint","IMPRINT",EDGE,{"derivedFrom":subQ0}),1.0]])]});}
            var Q22;
            {var subQ0=sQuery(id+"F0.wireOp",EDGE,"E4.24");Q22=makeQuery(id+"F0.imprint","IMPRINT",FACE,{"disambiguationData":[TD([[makeQuery(id+"F0.imprint","IMPRINT",EDGE,{"derivedFrom":subQ0}),1.0]])]});}
            var Q23;
            {var subQ0=sQuery(id+"F0.wireOp",EDGE,"E4.7");Q23=makeQuery(id+"F0.imprint","IMPRINT",FACE,{"disambiguationData":[TD([[makeQuery(id+"F0.imprint","IMPRINT",EDGE,{"derivedFrom":subQ0}),1.0]])]});}
            var Q24;
            {var subQ0=sQuery(id+"F0.wireOp",EDGE,"E4.20");Q24=makeQuery(id+"F0.imprint","IMPRINT",FACE,{"disambiguationData":[TD([[makeQuery(id+"F0.imprint","IMPRINT",EDGE,{"derivedFrom":subQ0}),1.0]])]});}
            var Q25;
            {var subQ3=sQuery(id+"F0.wireOp",EDGE,"E14");Q25=makeQuery(id+"F0.imprint","IMPRINT",FACE,{"disambiguationData":[TD([[makeQuery(id+"F0.imprint","IMPRINT",EDGE,{"derivedFrom":subQ3}),1.0]])]});}
            var Q26;
            {var subQ3=sQuery(id+"F0.wireOp",EDGE,"E8");Q26=makeQuery(id+"F0.imprint","IMPRINT",FACE,{"disambiguationData":[TD([[makeQuery(id+"F0.imprint","IMPRINT",EDGE,{"derivedFrom":subQ3}),1.0]])]});}
            var Q27;
            {var subQ3=sQuery(id+"F0.wireOp",EDGE,"E12");Q27=makeQuery(id+"F0.imprint","IMPRINT",FACE,{"disambiguationData":[TD([[makeQuery(id+"F0.imprint","IMPRINT",EDGE,{"derivedFrom":subQ3}),1.0]])]});}
            var Q28;
            {var subQ3=sQuery(id+"F0.wireOp",EDGE,"E26");Q28=makeQuery(id+"F0.imprint","IMPRINT",FACE,{"disambiguationData":[TD([[makeQuery(id+"F0.imprint","IMPRINT",EDGE,{"derivedFrom":subQ3}),1.0]])]});}
            var Q29;
            {var subQ0=sQuery(id+"F0.wireOp",EDGE,"E4.17");Q29=makeQuery(id+"F0.imprint","IMPRINT",FACE,{"disambiguationData":[TD([[makeQuery(id+"F0.imprint","IMPRINT",EDGE,{"derivedFrom":subQ0}),1.0]])]});}
            var Q30;
            {var subQ0=sQuery(id+"F0.wireOp",EDGE,"E4.5");Q30=makeQuery(id+"F0.imprint","IMPRINT",FACE,{"disambiguationData":[TD([[makeQuery(id+"F0.imprint","IMPRINT",EDGE,{"derivedFrom":subQ0}),1.0]])]});}
            var Q31;
            {var subQ3=sQuery(id+"F0.wireOp",EDGE,"E52");Q31=makeQuery(id+"F0.imprint","IMPRINT",FACE,{"disambiguationData":[TD([[makeQuery(id+"F0.imprint","IMPRINT",EDGE,{"derivedFrom":subQ3}),1.0]])]});}
            var Q32;
            {var subQ0=sQuery(id+"F0.wireOp",EDGE,"E4.13");Q32=makeQuery(id+"F0.imprint","IMPRINT",FACE,{"disambiguationData":[TD([[makeQuery(id+"F0.imprint","IMPRINT",EDGE,{"derivedFrom":subQ0}),1.0]])]});}
            var Q33;
            {var subQ3=sQuery(id+"F0.wireOp",EDGE,"E10");Q33=makeQuery(id+"F0.imprint","IMPRINT",FACE,{"disambiguationData":[TD([[makeQuery(id+"F0.imprint","IMPRINT",EDGE,{"derivedFrom":subQ3}),1.0]])]});}
            var Q34;
            {var subQ0=sQuery(id+"F0.wireOp",EDGE,"E4.10");Q34=makeQuery(id+"F0.imprint","IMPRINT",FACE,{"disambiguationData":[TD([[makeQuery(id+"F0.imprint","IMPRINT",EDGE,{"derivedFrom":subQ0}),1.0]])]});}
            var Q35;
            {var subQ0=sQuery(id+"F0.wireOp",EDGE,"E4.19");Q35=makeQuery(id+"F0.imprint","IMPRINT",FACE,{"disambiguationData":[TD([[makeQuery(id+"F0.imprint","IMPRINT",EDGE,{"derivedFrom":subQ0}),1.0]])]});}
            var Q36;
            {var subQ3=sQuery(id+"F0.wireOp",EDGE,"E44");Q36=makeQuery(id+"F0.imprint","IMPRINT",FACE,{"disambiguationData":[TD([[makeQuery(id+"F0.imprint","IMPRINT",EDGE,{"derivedFrom":subQ3}),1.0]])]});}
            var Q37;
            {var subQ0=sQuery(id+"F0.wireOp",EDGE,"E4.6");Q37=makeQuery(id+"F0.imprint","IMPRINT",FACE,{"disambiguationData":[TD([[makeQuery(id+"F0.imprint","IMPRINT",EDGE,{"derivedFrom":subQ0}),1.0]])]});}
            var Q38;
            {var subQ3=sQuery(id+"F0.wireOp",EDGE,"E28");Q38=makeQuery(id+"F0.imprint","IMPRINT",FACE,{"disambiguationData":[TD([[makeQuery(id+"F0.imprint","IMPRINT",EDGE,{"derivedFrom":subQ3}),1.0]])]});}
            var Q39;
            {var subQ3=sQuery(id+"F0.wireOp",EDGE,"E46");Q39=makeQuery(id+"F0.imprint","IMPRINT",FACE,{"disambiguationData":[TD([[makeQuery(id+"F0.imprint","IMPRINT",EDGE,{"derivedFrom":subQ3}),1.0]])]});}
            var Q40;
            {var subQ3=sQuery(id+"F0.wireOp",EDGE,"E6");Q40=makeQuery(id+"F0.imprint","IMPRINT",FACE,{"disambiguationData":[TD([[makeQuery(id+"F0.imprint","IMPRINT",EDGE,{"derivedFrom":subQ3}),-1.0]])]});}
            var Q41;
            Q41=makeQuery(id+"F1.opExtrude","CAP_FACE",FACE,{"disambiguationData":[OSD([sQuery(id+"F0.wireOp",EDGE,"E0"),sQuery(id+"F0.wireOp",EDGE,"E1")])],"isStart":false});
            var Q42;
            {var subQ0=sQuery(id+"F0.wireOp",EDGE,"E4.21");Q42=makeQuery(id+"F0.imprint","IMPRINT",FACE,{"disambiguationData":[TD([[makeQuery(id+"F0.imprint","IMPRINT",EDGE,{"derivedFrom":subQ0}),1.0]])]});}
            var Q43;
            {var subQ0=sQuery(id+"F0.wireOp",EDGE,"E4.14");Q43=makeQuery(id+"F0.imprint","IMPRINT",FACE,{"disambiguationData":[TD([[makeQuery(id+"F0.imprint","IMPRINT",EDGE,{"derivedFrom":subQ0}),1.0]])]});}
            var Q44;
            {var subQ0=sQuery(id+"F0.wireOp",EDGE,"E4.22");Q44=makeQuery(id+"F0.imprint","IMPRINT",FACE,{"disambiguationData":[TD([[makeQuery(id+"F0.imprint","IMPRINT",EDGE,{"derivedFrom":subQ0}),1.0]])]});}
            var Q45;
            {var subQ0=sQuery(id+"F0.wireOp",EDGE,"E4.12");Q45=makeQuery(id+"F0.imprint","IMPRINT",FACE,{"disambiguationData":[TD([[makeQuery(id+"F0.imprint","IMPRINT",EDGE,{"derivedFrom":subQ0}),1.0]])]});}
            var Q46;
            {var subQ0=sQuery(id+"F0.wireOp",EDGE,"E4.8");Q46=makeQuery(id+"F0.imprint","IMPRINT",FACE,{"disambiguationData":[TD([[makeQuery(id+"F0.imprint","IMPRINT",EDGE,{"derivedFrom":subQ0}),1.0]])]});}
            var Q47;
            {var subQ0=sQuery(id+"F0.wireOp",EDGE,"E4.16");Q47=makeQuery(id+"F0.imprint","IMPRINT",FACE,{"disambiguationData":[TD([[makeQuery(id+"F0.imprint","IMPRINT",EDGE,{"derivedFrom":subQ0}),1.0]])]});}
            var Q48;
            {var subQ0=sQuery(id+"F0.wireOp",EDGE,"E4.18");Q48=makeQuery(id+"F0.imprint","IMPRINT",FACE,{"disambiguationData":[TD([[makeQuery(id+"F0.imprint","IMPRINT",EDGE,{"derivedFrom":subQ0}),1.0]])]});}
            var Q49;
            {var subQ0=sQuery(id+"F0.wireOp",EDGE,"E4.11");Q49=makeQuery(id+"F0.imprint","IMPRINT",FACE,{"disambiguationData":[TD([[makeQuery(id+"F0.imprint","IMPRINT",EDGE,{"derivedFrom":subQ0}),1.0]])]});}
            var Q50;
            {var subQ0=sQuery(id+"F0.wireOp",EDGE,"E4.4");Q50=makeQuery(id+"F0.imprint","IMPRINT",FACE,{"disambiguationData":[TD([[makeQuery(id+"F0.imprint","IMPRINT",EDGE,{"derivedFrom":subQ0}),1.0]])]});}
            var Q51;
            {var subQ0=sQuery(id+"F0.wireOp",EDGE,"E4.15");Q51=makeQuery(id+"F0.imprint","IMPRINT",FACE,{"disambiguationData":[TD([[makeQuery(id+"F0.imprint","IMPRINT",EDGE,{"derivedFrom":subQ0}),1.0]])]});}
            var Q52;
            {var subQ0=sQuery(id+"F0.wireOp",EDGE,"E4.9");Q52=makeQuery(id+"F0.imprint","IMPRINT",FACE,{"disambiguationData":[TD([[makeQuery(id+"F0.imprint","IMPRINT",EDGE,{"derivedFrom":subQ0}),1.0]])]});}
            var Q53;
            {var subQ0=sQuery(id+"F0.wireOp",EDGE,"E4.2");Q53=makeQuery(id+"F0.imprint","IMPRINT",FACE,{"disambiguationData":[TD([[makeQuery(id+"F0.imprint","IMPRINT",EDGE,{"derivedFrom":subQ0}),1.0]])]});}
            var Q54;
            {var subQ0=sQuery(id+"F0.wireOp",EDGE,"E49");Q54=makeQuery(id+"F0.imprint","IMPRINT",FACE,{"disambiguationData":[TD([[makeQuery(id+"F0.imprint","IMPRINT",EDGE,{"derivedFrom":subQ0}),-1.0]])]});}
            var Q55;
            {var subQ0=sQuery(id+"F0.wireOp",EDGE,"E9");Q55=makeQuery(id+"F0.imprint","IMPRINT",FACE,{"disambiguationData":[TD([[makeQuery(id+"F0.imprint","IMPRINT",EDGE,{"derivedFrom":subQ0}),-1.0]])]});}
            var Q56;
            {var subQ0=sQuery(id+"F0.wireOp",EDGE,"E51");Q56=makeQuery(id+"F0.imprint","IMPRINT",FACE,{"disambiguationData":[TD([[makeQuery(id+"F0.imprint","IMPRINT",EDGE,{"derivedFrom":subQ0}),-1.0]])]});}
            var Q57;
            {var subQ0=sQuery(id+"F0.wireOp",EDGE,"E11");Q57=makeQuery(id+"F0.imprint","IMPRINT",FACE,{"disambiguationData":[TD([[makeQuery(id+"F0.imprint","IMPRINT",EDGE,{"derivedFrom":subQ0}),-1.0]])]});}
            var Q58;
            {var subQ0=sQuery(id+"F0.wireOp",EDGE,"E5");Q58=makeQuery(id+"F0.imprint","IMPRINT",FACE,{"disambiguationData":[TD([[makeQuery(id+"F0.imprint","IMPRINT",EDGE,{"derivedFrom":subQ0}),-1.0]])]});}
            var Q59;
            {var subQ0=sQuery(id+"F0.wireOp",EDGE,"E7");Q59=makeQuery(id+"F0.imprint","IMPRINT",FACE,{"disambiguationData":[TD([[makeQuery(id+"F0.imprint","IMPRINT",EDGE,{"derivedFrom":subQ0}),-1.0]])]});}
            var Q60;
            {var subQ2=sQuery(id+"F0.wireOp",EDGE,"E53");Q60=makeQuery(id+"F0.imprint","IMPRINT",FACE,{"disambiguationData":[TD([[makeQuery(id+"F0.imprint","IMPRINT",EDGE,{"derivedFrom":subQ2}),-1.0]])]});}
            extrude(context, id + "F3", {"entities" : qUnion([Q0, Q1, Q2, Q3, Q4, Q5, Q6, Q7, Q8, Q9, Q10, Q11, Q12, Q13, Q14, Q15, Q16, Q17, Q18, Q19, Q20, Q21, Q22, Q23, Q24, Q25, Q26, Q27, Q28, Q29, Q30, Q31, Q32, Q33, Q34, Q35, Q36, Q37, Q38, Q39, Q40, Q41, Q42, Q43, Q44, Q45, Q46, Q47, Q48, Q49, Q50, Q51, Q52, Q53, Q54, Q55, Q56, Q57, Q58, Q59, Q60]), "operationType" : NewBodyOperationType.ADD, "oppositeDirection" : true, "depth" : 1 * mm, "offsetDistance" : 25 * mm});
        }
    });
